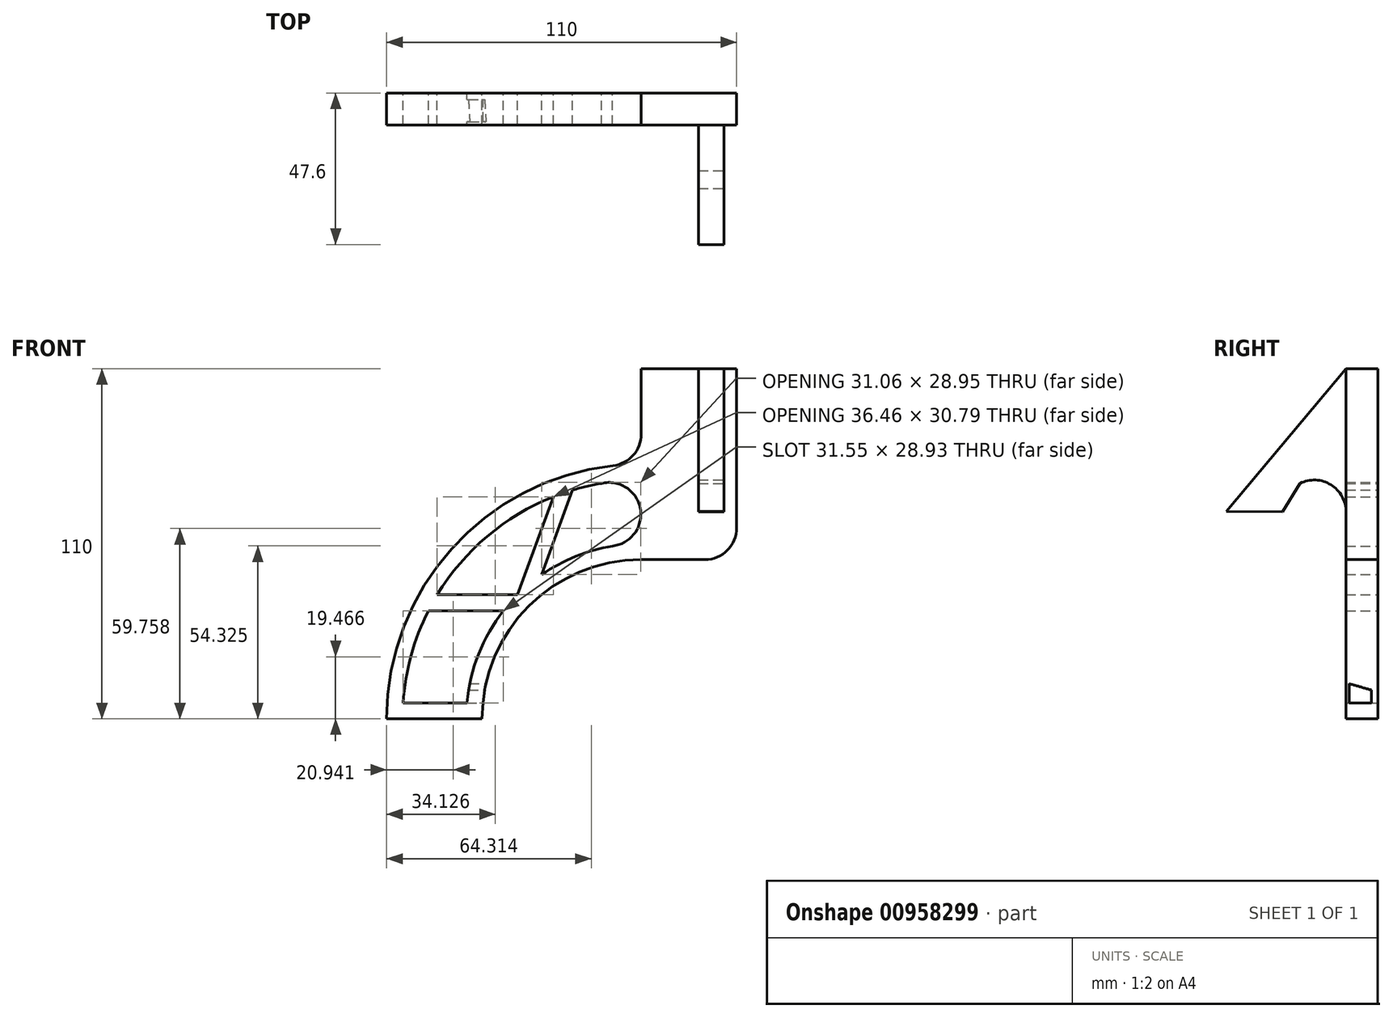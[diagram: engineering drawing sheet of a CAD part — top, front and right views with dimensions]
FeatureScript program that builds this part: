
annotation { "Feature Type Name" : "Feature", "Feature Type Description" : "" }
export const myFeature = defineFeature(function(context is Context, id is Id, definition is map)
    precondition{}
    {
        {
            var Q0;
            Q0=qCreatedBy(makeId("Front.planeOp"),FACE);
            var sketch = newSketch(context, id + "F0", { "sketchPlane" : qUnion([Q0])});
            skArc(sketch, "E0", {"start": v(0, 50) * mm, "mid": v(-35.36, 35.36) * mm, "end": v(-50, 0) * mm});
            skArc(sketch, "E1.0", {"start": v(-8.89, 79.5) * mm, "mid": v(-59.63, 53.33) * mm, "end": v(-80, 0) * mm});
            skLineSegment(sketch, "E2", {"start": v(-80, 0) * mm, "end": v(-50, 0) * mm});
            skLineSegment(sketch, "E3", {"start": v(-0.3, 80) * mm, "end": v(0, 50) * mm});
            skLineSegment(sketch, "E4.bottom", {"start": v(0, 50) * mm, "end": v(30, 50) * mm});
            skLineSegment(sketch, "E4.top", {"start": v(0, 110) * mm, "end": v(30, 110) * mm});
            skLineSegment(sketch, "E4.left", {"start": v(0, 89.44) * mm, "end": v(0, 110) * mm});
            skLineSegment(sketch, "E4.right", {"start": v(30, 50) * mm, "end": v(30, 110) * mm});
            skArc(sketch, "E5.0", {"start": v(0, 75) * mm, "mid": v(-51.23, 54.77) * mm, "end": v(-74.83, 5) * mm});
            skLineSegment(sketch, "E5.1", {"start": v(-74.83, 5) * mm, "end": v(-54.77, 5) * mm});
            skArc(sketch, "E5.2", {"start": v(-0.05, 55) * mm, "mid": v(-37.1, 40.6) * mm, "end": v(-54.77, 5) * mm});
            skLineSegment(sketch, "E6", {"start": v(-66.89, 33.93) * mm, "end": v(-43.29, 33.93) * mm});
            skLineSegment(sketch, "E7", {"start": v(-64.1, 38.93) * mm, "end": v(-38.85, 38.93) * mm});
            skLineSegment(sketch, "E8", {"start": v(-38.85, 38.93) * mm, "end": v(-27.64, 69.72) * mm});
            skLineSegment(sketch, "E9", {"start": v(-31.22, 45.28) * mm, "end": v(-21.55, 71.84) * mm});
            skArc(sketch, "E10", {"start": v(-0.15, 65) * mm, "mid": v(-4.26, 72.34) * mm, "end": v(-12.51, 73.95) * mm});
            skArc(sketch, "E11", {"start": v(-9, 54.26) * mm, "mid": v(-2.4, 57.84) * mm, "end": v(-0.15, 65) * mm});
            skArc(sketch, "E12.filletArc", {"start": v(-8.89, 79.5) * mm, "mid": v(-2.55, 82.78) * mm, "end": v(0, 89.44) * mm});
            skSolve(sketch);
        }
        {
            var Q0;
            {var subQ7=sQuery(id+"F0.wireOp",EDGE,"E0");Q0=makeQuery(id+"F0.imprint","IMPRINT",FACE,{"disambiguationData":[TD([[makeQuery(id+"F0.imprint","IMPRINT",EDGE,{"derivedFrom":subQ7}),-1.0]])]});}
            var Q1;
            {var subQ3=sQuery(id+"F0.wireOp",EDGE,"E4.bottom");Q1=makeQuery(id+"F0.imprint","IMPRINT",FACE,{"disambiguationData":[TD([[makeQuery(id+"F0.imprint","IMPRINT",EDGE,{"derivedFrom":subQ3}),1.0]])]});}
            var Q2;
            {var subQ0=sQuery(id+"F0.wireOp",EDGE,"E8");Q2=makeQuery(id+"F0.imprint","IMPRINT",FACE,{"disambiguationData":[TD([[makeQuery(id+"F0.imprint","IMPRINT",EDGE,{"derivedFrom":subQ0}),-1.0]])]});}
            var Q3;
            {var subQ0=sQuery(id+"F0.wireOp",EDGE,"E6");Q3=makeQuery(id+"F0.imprint","IMPRINT",FACE,{"disambiguationData":[TD([[makeQuery(id+"F0.imprint","IMPRINT",EDGE,{"derivedFrom":subQ0}),1.0]])]});}
            var Q4;
            {var subQ1=sQuery(id+"F0.wireOp",EDGE,"E3");var subQ3=sQuery(id+"F0.wireOp",EDGE,"E5.0");var subQ4=makeQuery(id+"F0.imprint","INTERSECT",VERTEX,{"derivedFrom":[subQ1,subQ3]});Q4=makeQuery(id+"F0.imprint","IMPRINT",FACE,{"disambiguationData":[TD([[makeQuery(id+"F0.imprint","IMPRINT",EDGE,{"disambiguationData":[TD([[subQ4,-1.0]])],"derivedFrom":subQ3}),1.0]])]});}
            var Q5;
            {var subQ0=sQuery(id+"F0.wireOp",EDGE,"E5.2");var subQ1=sQuery(id+"F0.wireOp",EDGE,"E3");var subQ2=makeQuery(id+"F0.imprint","INTERSECT",VERTEX,{"derivedFrom":[subQ1,subQ0]});Q5=makeQuery(id+"F0.imprint","IMPRINT",FACE,{"disambiguationData":[TD([[makeQuery(id+"F0.imprint","IMPRINT",EDGE,{"disambiguationData":[TD([[subQ2,1.0]])],"derivedFrom":subQ1}),-1.0]])]});}
            extrude(context, id + "F1", {"entities" : qUnion([Q0, Q1, Q2, Q3, Q4, Q5]), "depth" : 10 * mm, "offsetDistance" : 25 * mm});
        }
        {
            var Q0;
            Q0=makeQuery(id+"F1.opExtrude","SWEPT_EDGE",EDGE,{"disambiguationData":[OSD([sQuery(id+"F0.wireOp",EDGE,"E4.bottom"),sQuery(id+"F0.wireOp",EDGE,"E4.right")])]});
            fillet(context, id + "F2", {"entities" : qUnion([Q0]), "radius" : 10 * mm, "tangentPropagation" : true, "allowEdgeOverflow" : false});
        }
        {
            var Q0;
            Q0=qCreatedBy(makeId("Right.planeOp"),FACE);
            var sketch = newSketch(context, id + "F3", { "sketchPlane" : qUnion([Q0])});
            skLineSegment(sketch, "E13", {"start": v(-9, 5) * mm, "end": v(-2, 5) * mm});
            skLineSegment(sketch, "E14", {"start": v(-2, 5) * mm, "end": v(-2, 9) * mm});
            skLineSegment(sketch, "E15", {"start": v(-2, 9) * mm, "end": v(-9, 11) * mm});
            skLineSegment(sketch, "E16", {"start": v(-9, 11) * mm, "end": v(-9, 5) * mm});
            skSolve(sketch);
        }
        {
            var Q0;
            Q0=makeQuery(id+"F3.imprint","IMPRINT",FACE,{"disambiguationData":[TD([[makeQuery(id+"F3.imprint","IMPRINT",EDGE,{"derivedFrom":sQuery(id+"F3.wireOp",EDGE,"E13")}),1.0]])]});
            extrude(context, id + "F4", {"entities" : qUnion([Q0]), "operationType" : NewBodyOperationType.REMOVE, "oppositeDirection" : true, "depth" : 55 * mm, "offsetDistance" : 25 * mm});
        }
        {
            var Q0;
            Q0=makeQuery(id+"F1.opExtrude","SWEPT_FACE",FACE,{"disambiguationData":[OSD([sQuery(id+"F0.wireOp",EDGE,"E4.right")])]});
            var sketch = newSketch(context, id + "F5", { "sketchPlane" : qUnion([Q0])});
            skLineSegment(sketch, "E17", {"start": v(-10, 110) * mm, "end": v(-47.6, 65.19) * mm});
            skLineSegment(sketch, "E18", {"start": v(-10, 110) * mm, "end": v(-10, 65) * mm});
            skArc(sketch, "E19", {"start": v(-10, 65) * mm, "mid": v(-20, 75) * mm, "end": v(-30, 65) * mm});
            skLineSegment(sketch, "E20", {"start": v(-47.6, 65.19) * mm, "end": v(-30, 65) * mm});
            skFitSpline(sketch, "E21", {"points": [v(-24.46, 73.95) * mm, v(-30, 65) * mm], "startDerivative": vector(-5.55, -8.94) * mm, "endDerivative": vector(-5.55, -8.94) * mm});
            skSolve(sketch);
        }
        {
            var Q0;
            Q0=makeQuery(id+"F5.imprint","IMPRINT",FACE,{"disambiguationData":[TD([[makeQuery(id+"F5.imprint","IMPRINT",EDGE,{"derivedFrom":sQuery(id+"F5.wireOp",EDGE,"E17")}),1.0]])]});
            var Q1;
            {var subQ0=sQuery(id+"F5.wireOp",EDGE,"UvYYTOUm-OcNe-pfeu-MvD6-uuSAyu5PO5C0");Q1=makeQuery(id+"F5.imprint","IMPRINT",FACE,{"disambiguationData":[TD([[makeQuery(id+"F5.imprint","IMPRINT",EDGE,{"derivedFrom":subQ0}),1.0]])]});}
            var Q2;
            {var subQ0=sQuery(id+"F5.wireOp",EDGE,"E21");Q2=makeQuery(id+"F5.imprint","IMPRINT",FACE,{"disambiguationData":[TD([[makeQuery(id+"F5.imprint","IMPRINT",EDGE,{"derivedFrom":subQ0}),-1.0]])]});}
            extrude(context, id + "F6", {"entities" : qUnion([Q0, Q1, Q2]), "operationType" : NewBodyOperationType.ADD, "oppositeDirection" : true, "depth" : 12 * mm, "offsetDistance" : 25 * mm, "hasSecondDirection" : true, "secondDirectionOppositeDirection" : true, "secondDirectionDepth" : 4 * mm});
        }
    });
